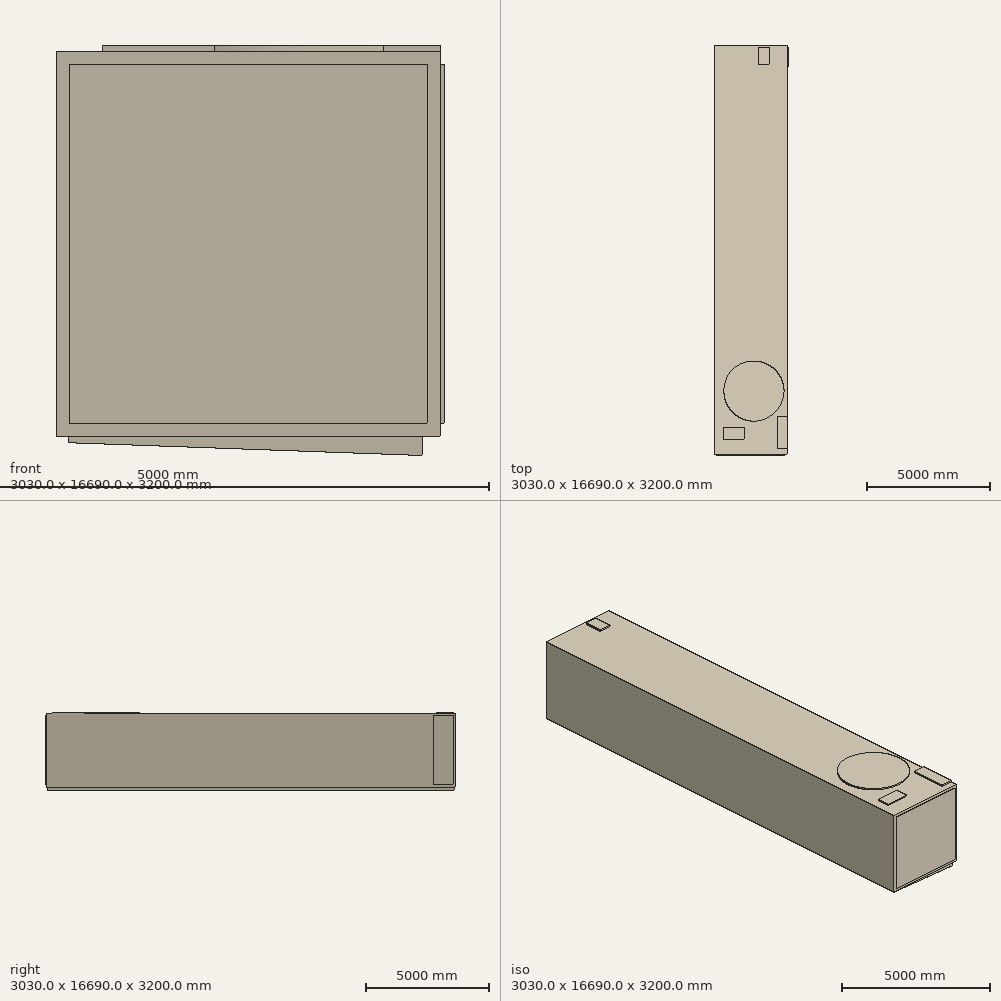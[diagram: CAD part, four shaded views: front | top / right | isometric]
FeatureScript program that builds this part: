
annotation { "Feature Type Name" : "Feature", "Feature Type Description" : "" }
export const myFeature = defineFeature(function(context is Context, id is Id, definition is map)
    precondition{}
    {
        {
            var Q0;
            Q0=qCreatedBy(makeId("Front.planeOp"),FACE);
            var sketch = newSketch(context, id + "F0", { "sketchPlane" : qUnion([Q0])});
            skLineSegment(sketch, "E0.bottom", {"start": v(1500, -1500) * mm, "end": v(-1500, -1500) * mm});
            skLineSegment(sketch, "E0.top", {"start": v(1500, 1500) * mm, "end": v(-1500, 1500) * mm});
            skLineSegment(sketch, "E0.left", {"start": v(1500, -1500) * mm, "end": v(1500, 1500) * mm});
            skLineSegment(sketch, "E0.right", {"start": v(-1500, -1500) * mm, "end": v(-1500, 1500) * mm});
            skPoint(sketch, "E0.middle", {"position": v(0, 0) * mm});
            skLineSegment(sketch, "E1.0", {"start": v(1400, 1400) * mm, "end": v(-1400, 1400) * mm});
            skLineSegment(sketch, "E1.1", {"start": v(1400, -1400) * mm, "end": v(1400, 1400) * mm});
            skLineSegment(sketch, "E1.2", {"start": v(1400, -1400) * mm, "end": v(-1400, -1400) * mm});
            skLineSegment(sketch, "E1.3", {"start": v(-1400, -1400) * mm, "end": v(-1400, 1400) * mm});
            skSolve(sketch);
        }
        {
            var Q0;
            Q0=makeQuery(id+"F0.imprint","IMPRINT",FACE,{"disambiguationData":[TD([[makeQuery(id+"F0.imprint","IMPRINT",EDGE,{"derivedFrom":sQuery(id+"F0.wireOp",EDGE,"E0.bottom")}),-1.0]])]});
            extrude(context, id + "F1", {"entities" : qUnion([Q0]), "oppositeDirection" : true, "depth" : 16660 * mm});
        }
        {
            var Q0;
            Q0=makeQuery(id+"F0.imprint","IMPRINT",FACE,{"disambiguationData":[TD([[makeQuery(id+"F0.imprint","IMPRINT",EDGE,{"derivedFrom":sQuery(id+"F0.wireOp",EDGE,"E1.0")}),1.0]])]});
            extrude(context, id + "F2", {"entities" : qUnion([Q0]), "depth" : 30 * mm});
        }
        {
            var Q0;
            Q0=makeQuery(id+"F0.imprint","IMPRINT",FACE,{"disambiguationData":[TD([[makeQuery(id+"F0.imprint","IMPRINT",EDGE,{"derivedFrom":sQuery(id+"F0.wireOp",EDGE,"E1.0")}),1.0]])]});
            var sketch = newSketch(context, id + "F3", { "sketchPlane" : qUnion([Q0])});
            skLineSegment(sketch, "E2.0", {"start": v(1500, -1500) * mm, "end": v(-1500, -1500) * mm});
            skLineSegment(sketch, "E3", {"start": v(-1406.2, -1500) * mm, "end": v(-1406.2, -1550) * mm});
            skLineSegment(sketch, "E4", {"start": v(-1406.2, -1550) * mm, "end": v(1359.76, -1650) * mm});
            skLineSegment(sketch, "E5", {"start": v(1359.76, -1650) * mm, "end": v(1359.76, -1500) * mm});
            skLineSegment(sketch, "E6", {"start": v(1359.76, -1500) * mm, "end": v(-1406.2, -1500) * mm});
            skSolve(sketch);
        }
        {
            var Q0;
            Q0 = qSketchRegion(id + "F3", true);
            var Q1;
            Q1=makeQuery(id+"F3.imprint","IMPRINT",FACE,{"disambiguationData":[TD([[makeQuery(id+"F3.imprint","IMPRINT",EDGE,{"derivedFrom":sQuery(id+"F3.wireOp",EDGE,"E3")}),1.0]])]});
            extrude(context, id + "F4", {"entities" : qUnion([Q0, Q1]), "operationType" : NewBodyOperationType.ADD, "oppositeDirection" : true, "depth" : 16619.6 * mm, "hasSecondDirection" : true, "secondDirectionOppositeDirection" : true, "secondDirectionDepth" : 49.47 * mm});
        }
        {
            var Q0;
            Q0=makeQuery(id+"F1.opExtrude","SWEPT_FACE",FACE,{"disambiguationData":[OSD([sQuery(id+"F0.wireOp",EDGE,"E0.top")])]});
            var sketch = newSketch(context, id + "F5", { "sketchPlane" : qUnion([Q0])});
            skLineSegment(sketch, "E7.bottom", {"start": v(1500, 0) * mm, "end": v(-1500, 0) * mm});
            skLineSegment(sketch, "E7.top", {"start": v(1500, 4000) * mm, "end": v(-1500, 4000) * mm});
            skLineSegment(sketch, "E7.left", {"start": v(1500, 0) * mm, "end": v(1500, 4000) * mm});
            skLineSegment(sketch, "E7.right", {"start": v(-1500, 0) * mm, "end": v(-1500, 4000) * mm});
            skLineSegment(sketch, "E8.bottom", {"start": v(1500, 244.43) * mm, "end": v(1054.64, 244.43) * mm});
            skLineSegment(sketch, "E8.top", {"start": v(1500, 1571.1) * mm, "end": v(1054.64, 1571.1) * mm});
            skLineSegment(sketch, "E8.left", {"start": v(1500, 244.43) * mm, "end": v(1500, 1571.1) * mm});
            skLineSegment(sketch, "E8.right", {"start": v(1054.64, 244.43) * mm, "end": v(1054.64, 1571.1) * mm});
            skLineSegment(sketch, "E9.bottom", {"start": v(-263.16, 1092.39) * mm, "end": v(-1143.16, 1092.39) * mm});
            skLineSegment(sketch, "E9.top", {"start": v(-263.16, 612.39) * mm, "end": v(-1143.16, 612.39) * mm});
            skLineSegment(sketch, "E9.left", {"start": v(-263.16, 1092.39) * mm, "end": v(-263.16, 612.39) * mm});
            skLineSegment(sketch, "E9.right", {"start": v(-1143.16, 1092.39) * mm, "end": v(-1143.16, 612.39) * mm});
            skCircle(sketch, "E10", {"center": v(115.64, 2591.25) * mm, "radius": 1225 * mm});
            skLineSegment(sketch, "E11.bottom", {"start": v(-1500, 16660) * mm, "end": v(1500, 16660) * mm});
            skLineSegment(sketch, "E11.top", {"start": v(-1500, 15760) * mm, "end": v(1500, 15760) * mm});
            skLineSegment(sketch, "E11.left", {"start": v(-1500, 16660) * mm, "end": v(-1500, 15760) * mm});
            skLineSegment(sketch, "E11.right", {"start": v(1500, 16660) * mm, "end": v(1500, 15760) * mm});
            skLineSegment(sketch, "E12.bottom", {"start": v(-1500, 15760) * mm, "end": v(221.33, 15760) * mm});
            skLineSegment(sketch, "E12.top", {"start": v(-1500, 16660) * mm, "end": v(221.33, 16660) * mm});
            skLineSegment(sketch, "E12.left", {"start": v(-1500, 15760) * mm, "end": v(-1500, 16660) * mm});
            skLineSegment(sketch, "E12.right", {"start": v(221.33, 15760) * mm, "end": v(221.33, 16660) * mm});
            skLineSegment(sketch, "E13.bottom", {"start": v(303.74, 16560.02) * mm, "end": v(756.95, 16560.02) * mm});
            skLineSegment(sketch, "E13.top", {"start": v(303.74, 15867.83) * mm, "end": v(756.95, 15867.83) * mm});
            skLineSegment(sketch, "E13.left", {"start": v(303.74, 16560.02) * mm, "end": v(303.74, 15867.83) * mm});
            skLineSegment(sketch, "E13.right", {"start": v(756.95, 16560.02) * mm, "end": v(756.95, 15867.83) * mm});
            skSolve(sketch);
        }
        {
            var Q0;
            Q0=makeQuery(id+"F5.imprint","IMPRINT",FACE,{"disambiguationData":[TD([[makeQuery(id+"F5.imprint","IMPRINT",EDGE,{"derivedFrom":sQuery(id+"F5.wireOp",EDGE,"E12.bottom")}),1.0]])]});
            var Q1;
            Q1=makeQuery(id+"F5.imprint","IMPRINT",FACE,{"disambiguationData":[TD([[makeQuery(id+"F5.imprint","IMPRINT",EDGE,{"derivedFrom":sQuery(id+"F5.wireOp",EDGE,"E9.bottom")}),1.0]])]});
            var Q2;
            Q2=makeQuery(id+"F5.imprint","IMPRINT",FACE,{"disambiguationData":[TD([[makeQuery(id+"F5.imprint","IMPRINT",EDGE,{"derivedFrom":sQuery(id+"F5.wireOp",EDGE,"E10")}),1.0]])]});
            var Q3;
            Q3=makeQuery(id+"F5.imprint","IMPRINT",FACE,{"disambiguationData":[TD([[makeQuery(id+"F5.imprint","IMPRINT",EDGE,{"derivedFrom":sQuery(id+"F5.wireOp",EDGE,"E8.bottom")}),-1.0]])]});
            var Q4;
            Q4=makeQuery(id+"F5.imprint","IMPRINT",FACE,{"disambiguationData":[TD([[makeQuery(id+"F5.imprint","IMPRINT",EDGE,{"derivedFrom":sQuery(id+"F5.wireOp",EDGE,"E13.bottom")}),-1.0]])]});
            extrude(context, id + "F6", {"entities" : qUnion([Q0, Q1, Q2, Q3, Q4]), "operationType" : NewBodyOperationType.ADD, "depth" : 50 * mm});
        }
        {
            var Q0;
            Q0=makeQuery(id+"F1.opExtrude","SWEPT_FACE",FACE,{"disambiguationData":[OSD([sQuery(id+"F0.wireOp",EDGE,"E0.left")])]});
            var sketch = newSketch(context, id + "F7", { "sketchPlane" : qUnion([Q0])});
            skLineSegment(sketch, "E14.bottom", {"start": v(16660, 1500) * mm, "end": v(15660, 1500) * mm});
            skLineSegment(sketch, "E14.top", {"start": v(16660, -1500) * mm, "end": v(15660, -1500) * mm});
            skLineSegment(sketch, "E14.left", {"start": v(16660, 1500) * mm, "end": v(16660, -1500) * mm});
            skLineSegment(sketch, "E14.right", {"start": v(15660, 1500) * mm, "end": v(15660, -1500) * mm});
            skLineSegment(sketch, "E15.0", {"start": v(16560, 1400) * mm, "end": v(15760, 1400) * mm});
            skLineSegment(sketch, "E15.1", {"start": v(16560, 1400) * mm, "end": v(16560, -1400) * mm});
            skLineSegment(sketch, "E15.2", {"start": v(16560, -1400) * mm, "end": v(15760, -1400) * mm});
            skLineSegment(sketch, "E15.3", {"start": v(15760, 1400) * mm, "end": v(15760, -1400) * mm});
            skLineSegment(sketch, "E16.0", {"start": v(16665, 1505) * mm, "end": v(-5, 1505) * mm});
            skLineSegment(sketch, "E16.1", {"start": v(16665, -1505) * mm, "end": v(16665, 1505) * mm});
            skLineSegment(sketch, "E16.2", {"start": v(-5, -1505) * mm, "end": v(16665, -1505) * mm});
            skLineSegment(sketch, "E16.3", {"start": v(-5, 1505) * mm, "end": v(-5, -1505) * mm});
            skSolve(sketch);
        }
        {
            var Q0;
            Q0=makeQuery(id+"F7.imprint","IMPRINT",FACE,{"disambiguationData":[TD([[makeQuery(id+"F7.imprint","IMPRINT",EDGE,{"derivedFrom":sQuery(id+"F7.wireOp",EDGE,"E15.0")}),1.0]])]});
            extrude(context, id + "F8", {"entities" : qUnion([Q0]), "operationType" : NewBodyOperationType.ADD, "depth" : 30 * mm});
        }
    });
